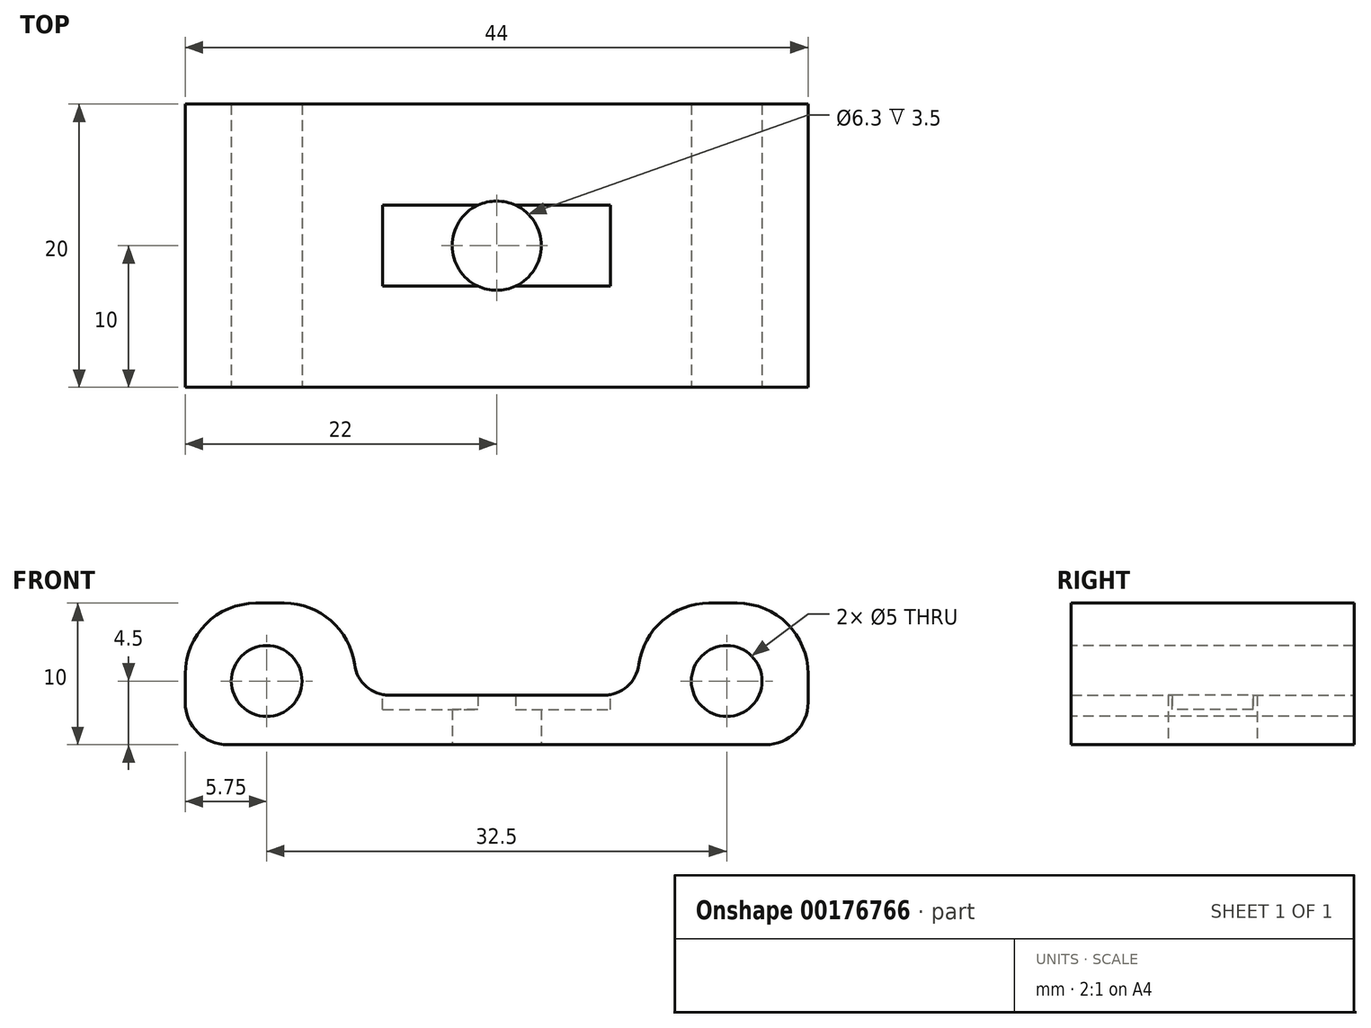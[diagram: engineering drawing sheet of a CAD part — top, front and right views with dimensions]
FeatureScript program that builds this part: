
annotation { "Feature Type Name" : "Feature", "Feature Type Description" : "" }
export const myFeature = defineFeature(function(context is Context, id is Id, definition is map)
    precondition{}
    {
        {
            var Q0;
            Q0=qCreatedBy(makeId("Top.planeOp"),FACE);
            var sketch = newSketch(context, id + "F0", { "sketchPlane" : qUnion([Q0])});
            skLineSegment(sketch, "E0.bottom", {"start": v(-18, 10) * mm, "end": v(18, 10) * mm});
            skLineSegment(sketch, "E0.top", {"start": v(-18, -10) * mm, "end": v(18, -10) * mm});
            skLineSegment(sketch, "E0.left", {"start": v(-18, 10) * mm, "end": v(-18, -10) * mm});
            skLineSegment(sketch, "E0.right", {"start": v(18, 10) * mm, "end": v(18, -10) * mm});
            skPoint(sketch, "E0.middle", {"position": v(0, 0) * mm});
            skLineSegment(sketch, "E1", {"start": v(-13, 0) * mm, "end": v(0, 0) * mm});
            skLineSegment(sketch, "E2", {"start": v(13, 0) * mm, "end": v(0, 0) * mm});
            skCircle(sketch, "E3", {"center": v(0, 0) * mm, "radius": 3.15 * mm});
            skSolve(sketch);
        }
        {
            var Q0;
            Q0=qSketchRegion(id+"F0",true);
            extrude(context, id + "F1", {"entities" : qUnion([Q0]), "depth" : 3.5 * mm, "offsetDistance" : 25 * mm});
        }
        {
            var Q0;
            Q0=makeQuery(id+"F1.opExtrude","CAP_FACE",FACE,{"disambiguationData":[OSD([sQuery(id+"F0.wireOp",EDGE,"E0.bottom"),sQuery(id+"F0.wireOp",EDGE,"E0.top"),sQuery(id+"F0.wireOp",EDGE,"E0.left"),sQuery(id+"F0.wireOp",EDGE,"E0.right"),sQuery(id+"F0.wireOp",EDGE,"xaLGl2y7-pWX8-Y6Ur-XBXW-NtWSVy60mo91"),sQuery(id+"F0.wireOp",EDGE,"5IJRBnyd-3dr1-AT0y-12cm-QC06rrJGliyf"),sQuery(id+"F0.wireOp",EDGE,"E3")])],"isStart":false});
            var sketch = newSketch(context, id + "F2", { "sketchPlane" : qUnion([Q0])});
            skLineSegment(sketch, "E4.bottom", {"start": v(-8.05, 2.85) * mm, "end": v(8.05, 2.85) * mm});
            skLineSegment(sketch, "E4.top", {"start": v(-8.05, -2.85) * mm, "end": v(8.05, -2.85) * mm});
            skLineSegment(sketch, "E4.left", {"start": v(-8.05, 2.85) * mm, "end": v(-8.05, -2.85) * mm});
            skLineSegment(sketch, "E4.right", {"start": v(8.05, 2.85) * mm, "end": v(8.05, -2.85) * mm});
            skPoint(sketch, "E4.middle", {"position": v(0, 0) * mm});
            skSolve(sketch);
        }
        {
            var Q0;
            Q0=makeQuery(id+"F2.imprint","IMPRINT",FACE,{"disambiguationData":[TD([[makeQuery(id+"F2.imprint","IMPRINT",EDGE,{"derivedFrom":sQuery(id+"F2.wireOp",EDGE,"E4.bottom")}),-1.0]])]});
            extrude(context, id + "F3", {"entities" : qUnion([Q0]), "operationType" : NewBodyOperationType.REMOVE, "oppositeDirection" : true, "depth" : 1 * mm});
        }
        {
            var Q0;
            Q0=qCreatedBy(makeId("Top.planeOp"),FACE);
            var sketch = newSketch(context, id + "F4", { "sketchPlane" : qUnion([Q0])});
            skLineSegment(sketch, "E5.bottom", {"start": v(18, 10) * mm, "end": v(22, 10) * mm});
            skLineSegment(sketch, "E5.top", {"start": v(18, -10) * mm, "end": v(22, -10) * mm});
            skLineSegment(sketch, "E5.left", {"start": v(18, 10) * mm, "end": v(18, -10) * mm});
            skLineSegment(sketch, "E5.right", {"start": v(22, 10) * mm, "end": v(22, -10) * mm});
            skLineSegment(sketch, "E6.MirrorCS", {"start": v(-18, 10) * mm, "end": v(-18, -10) * mm});
            skLineSegment(sketch, "E7.MirrorCS", {"start": v(-18, 10) * mm, "end": v(-22, 10) * mm});
            skLineSegment(sketch, "E8.MirrorCS", {"start": v(-18, -10) * mm, "end": v(-22, -10) * mm});
            skLineSegment(sketch, "E9.MirrorCS", {"start": v(-22, 10) * mm, "end": v(-22, -10) * mm});
            skPoint(sketch, "E10.centerSnap0", {"position": v(-18, 0) * mm});
            skLineSegment(sketch, "E11", {"start": v(-18, 10) * mm, "end": v(-10, 10) * mm});
            skLineSegment(sketch, "E12", {"start": v(-10, 10) * mm, "end": v(-10, -10) * mm});
            skLineSegment(sketch, "E13", {"start": v(-10, -10) * mm, "end": v(-18, -10) * mm});
            skLineSegment(sketch, "E14.MirrorCS", {"start": v(18, 10) * mm, "end": v(10, 10) * mm});
            skLineSegment(sketch, "E15.MirrorCS", {"start": v(10, -10) * mm, "end": v(18, -10) * mm});
            skLineSegment(sketch, "E16.MirrorCS", {"start": v(10, 10) * mm, "end": v(10, -10) * mm});
            skSolve(sketch);
        }
        {
            var Q0;
            Q0 = qSketchRegion(id + "F4", true);
            extrude(context, id + "F5", {"entities" : qUnion([Q0]), "operationType" : NewBodyOperationType.ADD, "depth" : 10 * mm, "offsetDistance" : 25 * mm});
        }
        {
            var Q0;
            Q0=makeQuery(id+"F5.boolean.opBoolean","MERGE",FACE,{"derivedFrom":[makeQuery(id+"F1.opExtrude","SWEPT_FACE",FACE,{"disambiguationData":[OSD([sQuery(id+"F0.wireOp",EDGE,"E0.top")])]}),makeQuery(id+"F5.opExtrude","SWEPT_FACE",FACE,{"disambiguationData":[OSD([sQuery(id+"F4.wireOp",EDGE,"E5.top"),sQuery(id+"F4.wireOp",EDGE,"E15.MirrorCS")])]}),makeQuery(id+"F5.opExtrude","SWEPT_FACE",FACE,{"disambiguationData":[OSD([sQuery(id+"F4.wireOp",EDGE,"E8.MirrorCS"),sQuery(id+"F4.wireOp",EDGE,"E13")])]})]});
            var sketch = newSketch(context, id + "F6", { "sketchPlane" : qUnion([Q0])});
            skCircle(sketch, "E17", {"center": v(-16.25, 4.5) * mm, "radius": 2.5 * mm});
            skCircle(sketch, "E18", {"center": v(16.25, 4.5) * mm, "radius": 2.5 * mm});
            skLineSegment(sketch, "E19", {"start": v(-16.25, 4.5) * mm, "end": v(16.25, 4.5) * mm});
            skPoint(sketch, "E20", {"position": v(0, 4.5) * mm});
            skSolve(sketch);
        }
        {
            var Q0;
            Q0 = qSketchRegion(id + "F6", true);
            extrude(context, id + "F7", {"entities" : qUnion([Q0]), "operationType" : NewBodyOperationType.REMOVE, "endBound" : BoundingType.THROUGH_ALL, "oppositeDirection" : true, "depth" : 25 * mm, "offsetDistance" : 25 * mm});
        }
        {
            var Q0;
            Q0=makeQuery(id+"F5.opExtrude","CAP_EDGE",EDGE,{"disambiguationData":[OSD([sQuery(id+"F4.wireOp",EDGE,"E9.MirrorCS")])],"isStart":false});
            var Q1;
            Q1=makeQuery(id+"F5.opExtrude","CAP_EDGE",EDGE,{"disambiguationData":[OSD([sQuery(id+"F4.wireOp",EDGE,"E12")])],"isStart":false});
            var Q2;
            Q2=makeQuery(id+"F5.opExtrude","CAP_EDGE",EDGE,{"disambiguationData":[OSD([sQuery(id+"F4.wireOp",EDGE,"E16.MirrorCS")])],"isStart":false});
            var Q3;
            Q3=makeQuery(id+"F5.opExtrude","CAP_EDGE",EDGE,{"disambiguationData":[OSD([sQuery(id+"F4.wireOp",EDGE,"E5.right")])],"isStart":false});
            fillet(context, id + "F8", {"entities" : qUnion([Q0, Q1, Q2, Q3]), "radius" : 5 * mm, "tangentPropagation" : true, "allowEdgeOverflow" : false});
        }
        {
            var Q0;
            Q0=makeQuery(id+"F5.opExtrude","CAP_EDGE",EDGE,{"disambiguationData":[OSD([sQuery(id+"F4.wireOp",EDGE,"E9.MirrorCS")])],"isStart":true});
            var Q1;
            Q1=makeQuery(id+"F5.opExtrude","CAP_EDGE",EDGE,{"disambiguationData":[OSD([sQuery(id+"F4.wireOp",EDGE,"E5.right")])],"isStart":true});
            fillet(context, id + "F9", {"entities" : qUnion([Q0, Q1]), "radius" : 3 * mm, "tangentPropagation" : true, "allowEdgeOverflow" : false});
        }
        {
            var Q0;
            Q0=makeQuery(id+"F5.boolean.opBoolean","INTERSECT",EDGE,{"derivedFrom":[makeQuery(id+"F1.opExtrude","CAP_FACE",FACE,{"disambiguationData":[OSD([sQuery(id+"F0.wireOp",EDGE,"E0.bottom"),sQuery(id+"F0.wireOp",EDGE,"E0.top"),sQuery(id+"F0.wireOp",EDGE,"E0.left"),sQuery(id+"F0.wireOp",EDGE,"E0.right"),sQuery(id+"F0.wireOp",EDGE,"E3")])],"isStart":false}),makeQuery(id+"F5.opExtrude","SWEPT_FACE",FACE,{"disambiguationData":[OSD([sQuery(id+"F4.wireOp",EDGE,"E16.MirrorCS")])]})]});
            var Q1;
            Q1=makeQuery(id+"F5.boolean.opBoolean","INTERSECT",EDGE,{"derivedFrom":[makeQuery(id+"F1.opExtrude","CAP_FACE",FACE,{"disambiguationData":[OSD([sQuery(id+"F0.wireOp",EDGE,"E0.bottom"),sQuery(id+"F0.wireOp",EDGE,"E0.top"),sQuery(id+"F0.wireOp",EDGE,"E0.left"),sQuery(id+"F0.wireOp",EDGE,"E0.right"),sQuery(id+"F0.wireOp",EDGE,"E3")])],"isStart":false}),makeQuery(id+"F5.opExtrude","SWEPT_FACE",FACE,{"disambiguationData":[OSD([sQuery(id+"F4.wireOp",EDGE,"E12")])]})]});
            fillet(context, id + "F10", {"entities" : qUnion([Q0, Q1]), "radius" : 2.5 * mm, "tangentPropagation" : true, "allowEdgeOverflow" : false});
        }
    });
